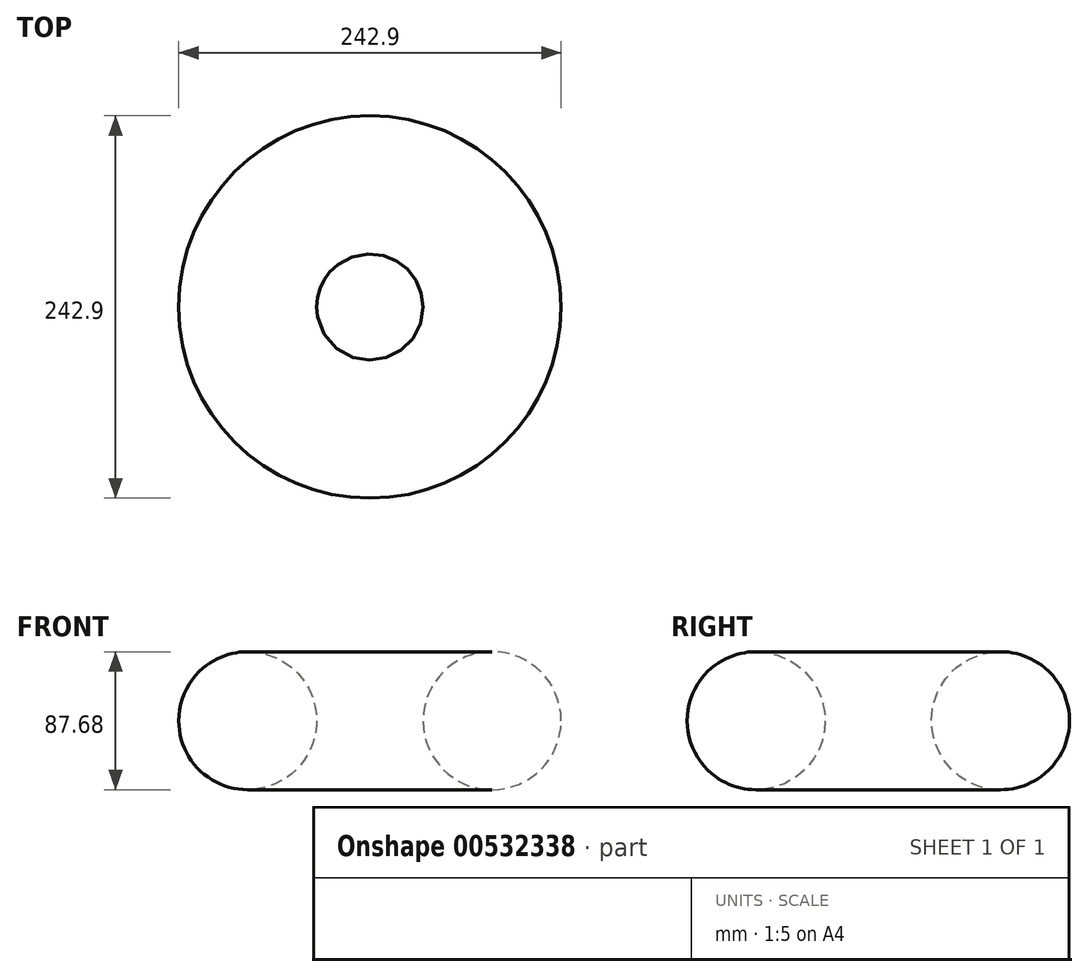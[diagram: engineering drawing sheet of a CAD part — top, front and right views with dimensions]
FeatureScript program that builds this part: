
annotation { "Feature Type Name" : "Feature", "Feature Type Description" : "" }
export const myFeature = defineFeature(function(context is Context, id is Id, definition is map)
    precondition{}
    {
        {
            var Q0;
            Q0=qCreatedBy(makeId("Right.planeOp"),FACE);
            var sketch = newSketch(context, id + "F0", { "sketchPlane" : qUnion([Q0])});
            skCircle(sketch, "E0", {"center": v(77.61, -53.82) * mm, "radius": 43.84 * mm});
            skLineSegment(sketch, "E1", {"start": v(0, 0) * mm, "end": v(0, -132.15) * mm});
            skSolve(sketch);
        }
        {
            var Q0;
            Q0=makeQuery(id+"F0.imprint","IMPRINT",FACE,{"disambiguationData":[TD([[makeQuery(id+"F0.imprint","IMPRINT",EDGE,{"derivedFrom":sQuery(id+"F0.wireOp",EDGE,"E0")}),1.0]])]});
            var Q1;
            Q1=sQuery(id+"F0.wireOp",EDGE,"E1");
            revolve(context, id + "F1", {"entities" : qUnion([Q0]), "axis" : qUnion([Q1]), "revolveType" : RevolveType.FULL});
        }
    });
